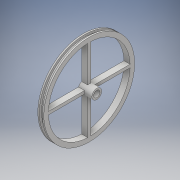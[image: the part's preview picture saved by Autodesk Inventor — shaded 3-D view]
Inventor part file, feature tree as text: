
AUTODESK INVENTOR PART (.ipt)
format: ipt  version: 2018 (Build 220112000, 112)  size: 329,216 bytes
history: native  units: mm
features: extrude x7, sketch x7, pattern_circular x1
ambient origin geometry x8: Origin, YZ Plane, XZ Plane, XY Plane, X Axis, Y Axis, Z Axis, Center Point
bodies: Solid1 (feature_tree)
feature tree (15):
  extrude  "Extrusion1"  Depth=2.0mm TaperAngle=0.0deg
  extrude  "Extrusion2"  Depth=1.0mm TaperAngle=0.0deg
  extrude  "Extrusion3"  Depth=1.0mm TaperAngle=0.0deg
  extrude  "Extrusion4"  Depth=10.0mm TaperAngle=0.0deg
  extrude  "Extrusion5"  Depth=6.5mm
  extrude  "Extrusion6"  Depth=1.0mm
  pattern_circular  "Circular Pattern1"  [2 undecoded]
  extrude  "Extrusion7"  Depth=5.0mm TaperAngle=360.0deg
  sketch  "Sketch1"  dims[d0=57.0mm d1=2.0mm d2=0.0mm]
  sketch  "Sketch2"  dims[d3=60.0mm d4=1.0mm d5=0.0mm]
  sketch  "Sketch3"  dims[d6=60.0mm d7=1.0mm d8=0.0mm]
  sketch  "Sketch4"  dims[d9=54.0mm d10=10.0mm d11=0.0mm]
  sketch  "Sketch5"  dims[d12=4.25mm d13=6.5mm]
  sketch  "Sketch6"  dims[d14=4.0mm d15=0.0mm d16=1.0mm]
  sketch  "Sketch7"  dims[d17=2.0mm d18=4.0mm d19=0.0mm d20=40.0mm d21=360.0deg d23=5.0mm d24=0.0mm]
note: 2 required parameter values undecoded (feature->parameter linkage not recoverable at this tier; creation-order binding heuristic only, values carry confidence <= 0.55)
